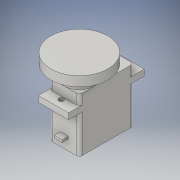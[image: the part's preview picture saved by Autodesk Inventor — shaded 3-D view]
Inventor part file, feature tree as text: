
AUTODESK INVENTOR PART (.ipt)
format: ipt  version: 2016 (Build 200138000, 138)  size: 165,376 bytes
history: native  units: in
note: dims shown in document units (in); Inventor stores cm internally (conversion verified against a paired STEP export)
features: extrude x5, sketch x5, plane x1
ambient origin geometry x8: Origin, YZ Plane, XZ Plane, XY Plane, X Axis, Y Axis, Z Axis, Center Point
bodies: Solid1 (feature_tree)
feature tree (11):
  extrude  "Extrusion1"  Depth=0.9in
  extrude  "Extrusion2"  Depth=0.9in TaperAngle=0.0deg
  extrude  "Extrusion3"  Depth=0.2in
  plane  "Work Plane1"
  extrude  "Extrusion4"  [1 undecoded]
  extrude  "Extrusion5"  Depth=0.08in
  sketch  "Sketch1"  dims[d0=0.5in d1=0.9in]
  sketch  "Sketch2"  dims[d2=0.05in d3=0.9in d4=0.0in]
  sketch  "Sketch3"  dims[d7=0.2in d8=0.0in d9=0.95in]
  sketch  "Sketch5"  dims[d10=0.16in d11=0.0in d12=-0.17in]
  sketch  "Sketch6"  dims[d13=0.63in d14=0.08in d15=1.0in d16=0.1in d17=0.0in d18=0.13in d19=0.04in d20=0.17in d21=0.1in d22=0.0in]
note: 1 required parameter value undecoded (feature->parameter linkage not recoverable at this tier; creation-order binding heuristic only, values carry confidence <= 0.55)
